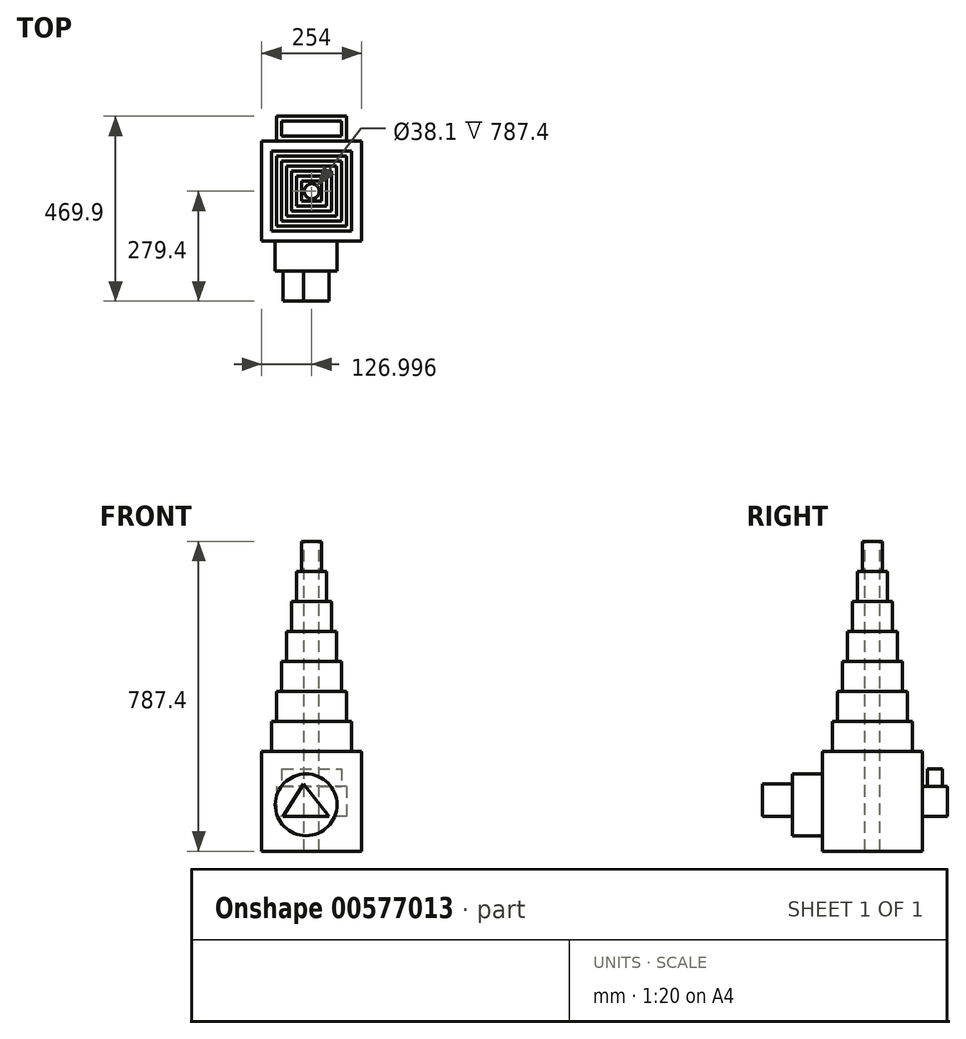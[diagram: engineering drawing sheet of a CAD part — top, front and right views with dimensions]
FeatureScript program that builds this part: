
annotation { "Feature Type Name" : "Feature", "Feature Type Description" : "" }
export const myFeature = defineFeature(function(context is Context, id is Id, definition is map)
    precondition{}
    {
        {
            var Q0;
            Q0=qCreatedBy(makeId("Front.planeOp"),FACE);
            var sketch = newSketch(context, id + "F0", { "sketchPlane" : qUnion([Q0])});
            skLineSegment(sketch, "E0.bottom", {"start": v(-94.27, 165.73) * mm, "end": v(159.73, 165.73) * mm});
            skLineSegment(sketch, "E0.top", {"start": v(-94.27, -88.27) * mm, "end": v(159.73, -88.27) * mm});
            skLineSegment(sketch, "E0.left", {"start": v(-94.27, 165.73) * mm, "end": v(-94.27, -88.27) * mm});
            skLineSegment(sketch, "E0.right", {"start": v(159.73, 165.73) * mm, "end": v(159.73, -88.27) * mm});
            skSolve(sketch);
        }
        {
            var Q0;
            Q0 = qSketchRegion(id + "F0", true);
            extrude(context, id + "F1", {"entities" : qUnion([Q0]), "depth" : 254 * mm, "offsetDistance" : 25.4 * mm});
        }
        {
            var Q0;
            Q0=makeQuery(id+"F1.opExtrude","CAP_FACE",FACE,{"disambiguationData":[OSD([sQuery(id+"F0.wireOp",EDGE,"E0.bottom"),sQuery(id+"F0.wireOp",EDGE,"E0.top"),sQuery(id+"F0.wireOp",EDGE,"E0.left"),sQuery(id+"F0.wireOp",EDGE,"E0.right")])],"isStart":false});
            var sketch = newSketch(context, id + "F2", { "sketchPlane" : qUnion([Q0])});
            skCircle(sketch, "E1", {"center": v(18.44, 29.72) * mm, "radius": 78.38 * mm});
            skSolve(sketch);
        }
        {
            var Q0;
            Q0=makeQuery(id+"F1.opExtrude","SWEPT_FACE",FACE,{"disambiguationData":[OSD([sQuery(id+"F0.wireOp",EDGE,"E0.bottom")])]});
            var sketch = newSketch(context, id + "F3", { "sketchPlane" : qUnion([Q0])});
            skLineSegment(sketch, "E2.bottom", {"start": v(-68.87, -25.4) * mm, "end": v(134.33, -25.4) * mm});
            skLineSegment(sketch, "E2.top", {"start": v(-68.87, -228.6) * mm, "end": v(134.33, -228.6) * mm});
            skLineSegment(sketch, "E2.left", {"start": v(-68.87, -25.4) * mm, "end": v(-68.87, -228.6) * mm});
            skLineSegment(sketch, "E2.right", {"start": v(134.33, -25.4) * mm, "end": v(134.33, -228.6) * mm});
            skSolve(sketch);
        }
        {
            var Q0;
            Q0=makeQuery(id+"F3.imprint","IMPRINT",FACE,{"disambiguationData":[TD([[makeQuery(id+"F3.imprint","IMPRINT",EDGE,{"derivedFrom":sQuery(id+"F3.wireOp",EDGE,"E2.bottom")}),-1.0]])]});
            extrude(context, id + "F4", {"entities" : qUnion([Q0]), "operationType" : NewBodyOperationType.ADD, "depth" : 76.2 * mm, "offsetDistance" : 25.4 * mm});
        }
        {
            var Q0;
            Q0=makeQuery(id+"F4.opExtrude","CAP_FACE",FACE,{"disambiguationData":[OSD([sQuery(id+"F3.wireOp",EDGE,"E2.bottom"),sQuery(id+"F3.wireOp",EDGE,"E2.top"),sQuery(id+"F3.wireOp",EDGE,"E2.left"),sQuery(id+"F3.wireOp",EDGE,"E2.right")])],"isStart":false});
            var sketch = newSketch(context, id + "F5", { "sketchPlane" : qUnion([Q0])});
            skLineSegment(sketch, "E3.bottom", {"start": v(-56.17, -38.1) * mm, "end": v(121.63, -38.1) * mm});
            skLineSegment(sketch, "E3.top", {"start": v(-56.17, -215.9) * mm, "end": v(121.63, -215.9) * mm});
            skLineSegment(sketch, "E3.left", {"start": v(-56.17, -38.1) * mm, "end": v(-56.17, -215.9) * mm});
            skLineSegment(sketch, "E3.right", {"start": v(121.63, -38.1) * mm, "end": v(121.63, -215.9) * mm});
            skSolve(sketch);
        }
        {
            var Q0;
            Q0=makeQuery(id+"F5.imprint","IMPRINT",FACE,{"disambiguationData":[TD([[makeQuery(id+"F5.imprint","IMPRINT",EDGE,{"derivedFrom":sQuery(id+"F5.wireOp",EDGE,"E3.bottom")}),-1.0]])]});
            extrude(context, id + "F6", {"entities" : qUnion([Q0]), "operationType" : NewBodyOperationType.ADD, "depth" : 76.2 * mm, "offsetDistance" : 25.4 * mm});
        }
        {
            var Q0;
            Q0=makeQuery(id+"F6.opExtrude","CAP_FACE",FACE,{"disambiguationData":[OSD([sQuery(id+"F5.wireOp",EDGE,"E3.bottom"),sQuery(id+"F5.wireOp",EDGE,"E3.top"),sQuery(id+"F5.wireOp",EDGE,"E3.left"),sQuery(id+"F5.wireOp",EDGE,"E3.right")])],"isStart":false});
            var sketch = newSketch(context, id + "F7", { "sketchPlane" : qUnion([Q0])});
            skLineSegment(sketch, "E4.bottom", {"start": v(-43.47, -50.8) * mm, "end": v(108.93, -50.8) * mm});
            skLineSegment(sketch, "E4.top", {"start": v(-43.47, -203.2) * mm, "end": v(108.93, -203.2) * mm});
            skLineSegment(sketch, "E4.left", {"start": v(-43.47, -50.8) * mm, "end": v(-43.47, -203.2) * mm});
            skLineSegment(sketch, "E4.right", {"start": v(108.93, -50.8) * mm, "end": v(108.93, -203.2) * mm});
            skSolve(sketch);
        }
        {
            var Q0;
            Q0=makeQuery(id+"F7.imprint","IMPRINT",FACE,{"disambiguationData":[TD([[makeQuery(id+"F7.imprint","IMPRINT",EDGE,{"derivedFrom":sQuery(id+"F7.wireOp",EDGE,"E4.bottom")}),-1.0]])]});
            extrude(context, id + "F8", {"entities" : qUnion([Q0]), "operationType" : NewBodyOperationType.ADD, "depth" : 76.2 * mm, "offsetDistance" : 25.4 * mm});
        }
        {
            var Q0;
            Q0=makeQuery(id+"F8.opExtrude","CAP_FACE",FACE,{"disambiguationData":[OSD([sQuery(id+"F7.wireOp",EDGE,"E4.bottom"),sQuery(id+"F7.wireOp",EDGE,"E4.top"),sQuery(id+"F7.wireOp",EDGE,"E4.left"),sQuery(id+"F7.wireOp",EDGE,"E4.right")])],"isStart":false});
            var sketch = newSketch(context, id + "F9", { "sketchPlane" : qUnion([Q0])});
            skLineSegment(sketch, "E5.bottom", {"start": v(-30.77, -63.5) * mm, "end": v(96.23, -63.5) * mm});
            skLineSegment(sketch, "E5.top", {"start": v(-30.77, -190.5) * mm, "end": v(96.23, -190.5) * mm});
            skLineSegment(sketch, "E5.left", {"start": v(-30.77, -63.5) * mm, "end": v(-30.77, -190.5) * mm});
            skLineSegment(sketch, "E5.right", {"start": v(96.23, -63.5) * mm, "end": v(96.23, -190.5) * mm});
            skSolve(sketch);
        }
        {
            var Q0;
            Q0=makeQuery(id+"F9.imprint","IMPRINT",FACE,{"disambiguationData":[TD([[makeQuery(id+"F9.imprint","IMPRINT",EDGE,{"derivedFrom":sQuery(id+"F9.wireOp",EDGE,"E5.bottom")}),-1.0]])]});
            extrude(context, id + "F10", {"entities" : qUnion([Q0]), "operationType" : NewBodyOperationType.ADD, "depth" : 76.2 * mm, "offsetDistance" : 25.4 * mm});
        }
        {
            var Q0;
            Q0=makeQuery(id+"F10.opExtrude","CAP_FACE",FACE,{"disambiguationData":[OSD([sQuery(id+"F9.wireOp",EDGE,"E5.bottom"),sQuery(id+"F9.wireOp",EDGE,"E5.top"),sQuery(id+"F9.wireOp",EDGE,"E5.left"),sQuery(id+"F9.wireOp",EDGE,"E5.right")])],"isStart":false});
            var sketch = newSketch(context, id + "F11", { "sketchPlane" : qUnion([Q0])});
            skLineSegment(sketch, "E6.bottom", {"start": v(-18.07, -76.2) * mm, "end": v(83.53, -76.2) * mm});
            skLineSegment(sketch, "E6.top", {"start": v(-18.07, -177.8) * mm, "end": v(83.53, -177.8) * mm});
            skLineSegment(sketch, "E6.left", {"start": v(-18.07, -76.2) * mm, "end": v(-18.07, -177.8) * mm});
            skLineSegment(sketch, "E6.right", {"start": v(83.53, -76.2) * mm, "end": v(83.53, -177.8) * mm});
            skSolve(sketch);
        }
        {
            var Q0;
            Q0 = qSketchRegion(id + "F11", true);
            extrude(context, id + "F12", {"entities" : qUnion([Q0]), "operationType" : NewBodyOperationType.ADD, "depth" : 76.2 * mm, "offsetDistance" : 25.4 * mm});
        }
        {
            var Q0;
            Q0=makeQuery(id+"F12.opExtrude","CAP_FACE",FACE,{"disambiguationData":[OSD([sQuery(id+"F11.wireOp",EDGE,"E6.bottom"),sQuery(id+"F11.wireOp",EDGE,"E6.top"),sQuery(id+"F11.wireOp",EDGE,"E6.left"),sQuery(id+"F11.wireOp",EDGE,"E6.right")])],"isStart":false});
            var sketch = newSketch(context, id + "F13", { "sketchPlane" : qUnion([Q0])});
            skLineSegment(sketch, "E7.bottom", {"start": v(-5.37, -88.9) * mm, "end": v(70.83, -88.9) * mm});
            skLineSegment(sketch, "E7.top", {"start": v(-5.37, -165.1) * mm, "end": v(70.83, -165.1) * mm});
            skLineSegment(sketch, "E7.left", {"start": v(-5.37, -88.9) * mm, "end": v(-5.37, -165.1) * mm});
            skLineSegment(sketch, "E7.right", {"start": v(70.83, -88.9) * mm, "end": v(70.83, -165.1) * mm});
            skSolve(sketch);
        }
        {
            var Q0;
            Q0 = qSketchRegion(id + "F13", true);
            extrude(context, id + "F14", {"entities" : qUnion([Q0]), "operationType" : NewBodyOperationType.ADD, "depth" : 76.2 * mm, "offsetDistance" : 25.4 * mm});
        }
        {
            var Q0;
            Q0=makeQuery(id+"F14.opExtrude","CAP_FACE",FACE,{"disambiguationData":[OSD([sQuery(id+"F13.wireOp",EDGE,"E7.bottom"),sQuery(id+"F13.wireOp",EDGE,"E7.top"),sQuery(id+"F13.wireOp",EDGE,"E7.left"),sQuery(id+"F13.wireOp",EDGE,"E7.right")])],"isStart":false});
            var sketch = newSketch(context, id + "F15", { "sketchPlane" : qUnion([Q0])});
            skLineSegment(sketch, "E8.bottom", {"start": v(58.13, -101.6) * mm, "end": v(7.33, -101.6) * mm});
            skLineSegment(sketch, "E8.top", {"start": v(58.13, -152.4) * mm, "end": v(7.33, -152.4) * mm});
            skLineSegment(sketch, "E8.left", {"start": v(58.13, -101.6) * mm, "end": v(58.13, -152.4) * mm});
            skLineSegment(sketch, "E8.right", {"start": v(7.33, -101.6) * mm, "end": v(7.33, -152.4) * mm});
            skSolve(sketch);
        }
        {
            var Q0;
            Q0 = qSketchRegion(id + "F15", true);
            extrude(context, id + "F16", {"entities" : qUnion([Q0]), "operationType" : NewBodyOperationType.ADD, "depth" : 76.2 * mm, "offsetDistance" : 25.4 * mm});
        }
        {
            var Q0;
            Q0=makeQuery(id+"F16.opExtrude","CAP_FACE",FACE,{"disambiguationData":[OSD([sQuery(id+"F15.wireOp",EDGE,"E8.bottom"),sQuery(id+"F15.wireOp",EDGE,"E8.top"),sQuery(id+"F15.wireOp",EDGE,"E8.left"),sQuery(id+"F15.wireOp",EDGE,"E8.right")])],"isStart":false});
            var sketch = newSketch(context, id + "F17", { "sketchPlane" : qUnion([Q0])});
            skPoint(sketch, "E9", {"position": v(32.73, -127) * mm});
            skSolve(sketch);
        }
        {
            var Q0;
            Q0=sQuery(id+"F17.wireOp",VERTEX,"E9");
            var Q1;
            Q1=makeQuery(id+"F1.opExtrude","SWEPT_BODY",BODY,{"disambiguationData":[OSD([sQuery(id+"F0.wireOp",EDGE,"E0.bottom"),sQuery(id+"F0.wireOp",EDGE,"E0.top"),sQuery(id+"F0.wireOp",EDGE,"E0.left"),sQuery(id+"F0.wireOp",EDGE,"E0.right")])]});
            hole(context, id + "F18", {"style" : HoleStyle.SIMPLE, "endStyle" : HoleEndStyle.THROUGH, "holeDiameter" : 38.1 * mm, "isTappedThrough" : true, "tappedDepth" : 12.7 * mm, "tapClearance" : 3, "locations" : qUnion([Q0]), "scope" : qUnion([Q1])});
        }
        {
            var Q0;
            Q0 = qSketchRegion(id + "F2", true);
            extrude(context, id + "F19", {"entities" : qUnion([Q0]), "operationType" : NewBodyOperationType.ADD, "depth" : 76.2 * mm, "offsetDistance" : 25.4 * mm});
        }
        {
            var Q0;
            Q0=makeQuery(id+"F19.opExtrude","CAP_FACE",FACE,{"disambiguationData":[OSD([sQuery(id+"F2.wireOp",EDGE,"E1")])],"isStart":false});
            var sketch = newSketch(context, id + "F20", { "sketchPlane" : qUnion([Q0])});
            skLineSegment(sketch, "E10", {"start": v(12.23, 82.34) * mm, "end": v(-40.13, 0) * mm});
            skLineSegment(sketch, "E11", {"start": v(-40.13, 0) * mm, "end": v(77.02, 0) * mm});
            skLineSegment(sketch, "E12", {"start": v(77.02, 0) * mm, "end": v(12.23, 82.34) * mm});
            skSolve(sketch);
        }
        {
            var Q0;
            Q0 = qSketchRegion(id + "F20", true);
            extrude(context, id + "F21", {"entities" : qUnion([Q0]), "operationType" : NewBodyOperationType.ADD, "depth" : 76.2 * mm, "offsetDistance" : 25.4 * mm});
        }
        {
            var Q0;
            Q0=makeQuery(id+"F1.opExtrude","CAP_FACE",FACE,{"disambiguationData":[OSD([sQuery(id+"F0.wireOp",EDGE,"E0.bottom"),sQuery(id+"F0.wireOp",EDGE,"E0.top"),sQuery(id+"F0.wireOp",EDGE,"E0.left"),sQuery(id+"F0.wireOp",EDGE,"E0.right")])],"isStart":true});
            var sketch = newSketch(context, id + "F22", { "sketchPlane" : qUnion([Q0])});
            skLineSegment(sketch, "E13.bottom", {"start": v(-121.63, 76.83) * mm, "end": v(56.17, 76.83) * mm});
            skLineSegment(sketch, "E13.top", {"start": v(-121.63, 0.63) * mm, "end": v(56.17, 0.63) * mm});
            skLineSegment(sketch, "E13.left", {"start": v(-121.63, 76.83) * mm, "end": v(-121.63, 0.63) * mm});
            skLineSegment(sketch, "E13.right", {"start": v(56.17, 76.83) * mm, "end": v(56.17, 0.63) * mm});
            skSolve(sketch);
        }
        {
            var Q0;
            Q0 = qSketchRegion(id + "F22", true);
            extrude(context, id + "F23", {"entities" : qUnion([Q0]), "operationType" : NewBodyOperationType.ADD, "depth" : 63.5 * mm, "offsetDistance" : 25.4 * mm});
        }
        {
            var Q0;
            Q0=makeQuery(id+"F23.opExtrude","SWEPT_FACE",FACE,{"disambiguationData":[OSD([sQuery(id+"F22.wireOp",EDGE,"E13.bottom")])]});
            var sketch = newSketch(context, id + "F24", { "sketchPlane" : qUnion([Q0])});
            skSolve(sketch);
        }
        {
            var Q0;
            {var subQ0=sQuery(id+"F22.wireOp",EDGE,"E13.bottom");Q0=makeQuery(id+"F24.imprint","IMPRINT",FACE,{"disambiguationData":[TD([[makeQuery(id+"F24.imprint","IMPRINT",EDGE,{"derivedFrom":makeQuery(id+"F23.opExtrude","CAP_EDGE",EDGE,{"disambiguationData":[OSD([subQ0])],"isStart":false})}),1.0]])]});}
            var sketch = newSketch(context, id + "F25", { "sketchPlane" : qUnion([Q0])});
            skLineSegment(sketch, "E14.bottom", {"start": v(-43.47, 50.8) * mm, "end": v(108.93, 50.8) * mm});
            skLineSegment(sketch, "E14.top", {"start": v(-43.47, 12.7) * mm, "end": v(108.93, 12.7) * mm});
            skLineSegment(sketch, "E14.left", {"start": v(-43.47, 50.8) * mm, "end": v(-43.47, 12.7) * mm});
            skLineSegment(sketch, "E14.right", {"start": v(108.93, 50.8) * mm, "end": v(108.93, 12.7) * mm});
            skSolve(sketch);
        }
        {
            var Q0;
            Q0 = qSketchRegion(id + "F25", true);
            extrude(context, id + "F26", {"entities" : qUnion([Q0]), "operationType" : NewBodyOperationType.ADD, "depth" : 44.45 * mm, "offsetDistance" : 25.4 * mm});
        }
    });
